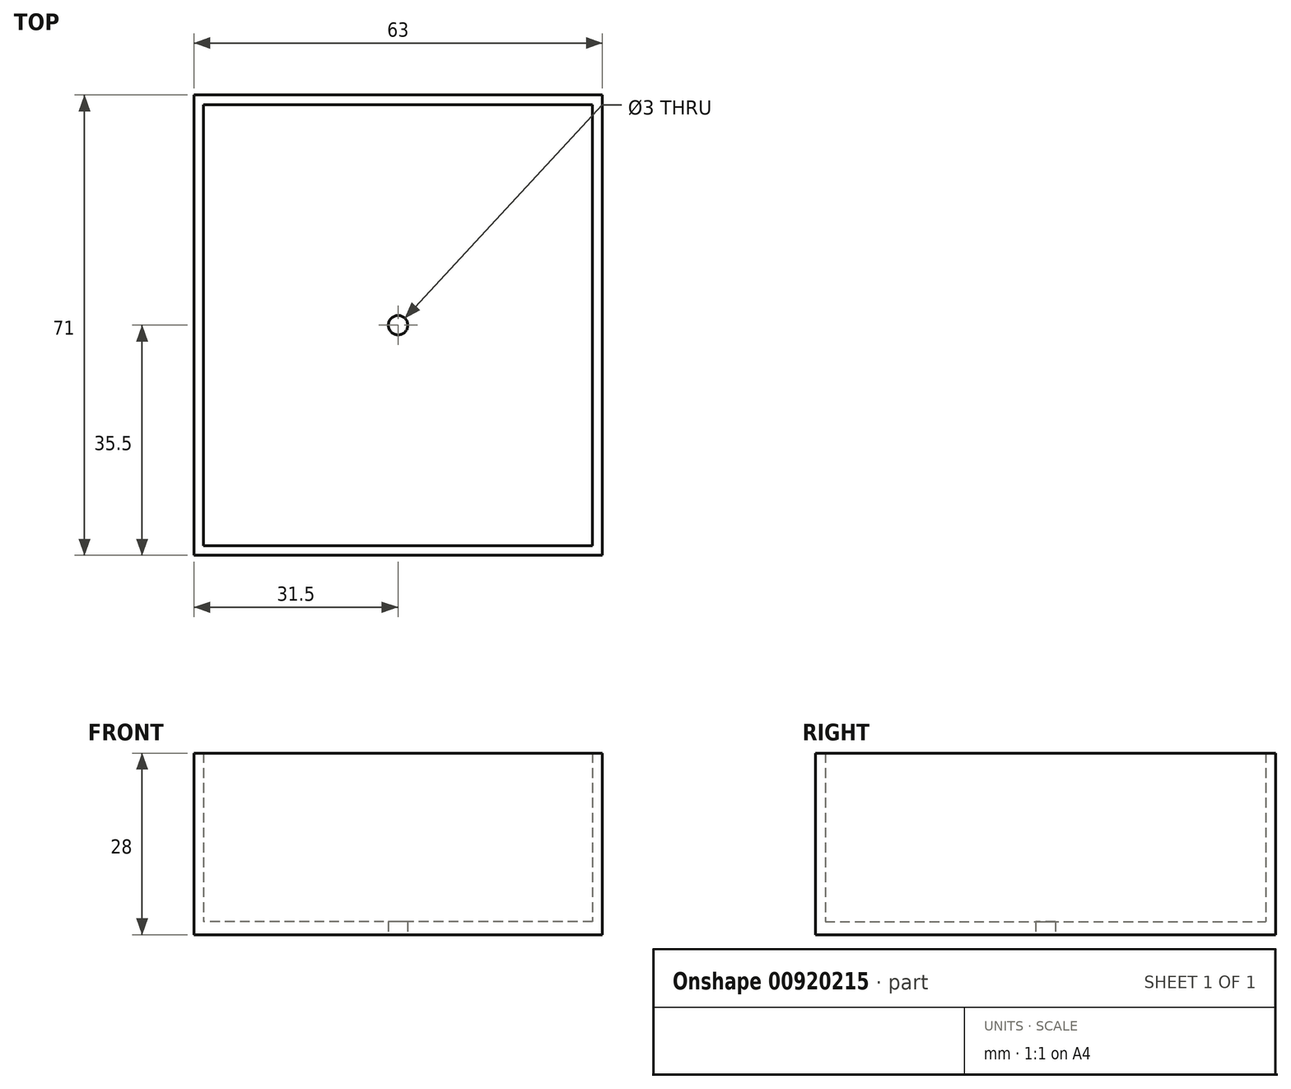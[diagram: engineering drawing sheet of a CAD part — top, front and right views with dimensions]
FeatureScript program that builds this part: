
annotation { "Feature Type Name" : "Feature", "Feature Type Description" : "" }
export const myFeature = defineFeature(function(context is Context, id is Id, definition is map)
    precondition{}
    {
        {
            var Q0;
            Q0=qCreatedBy(makeId("Top.planeOp"),FACE);
            var sketch = newSketch(context, id + "F0", { "sketchPlane" : qUnion([Q0])});
            skLineSegment(sketch, "E0.bottom", {"start": v(-30, 34) * mm, "end": v(30, 34) * mm});
            skLineSegment(sketch, "E0.top", {"start": v(-30, -34) * mm, "end": v(30, -34) * mm});
            skLineSegment(sketch, "E0.left", {"start": v(-30, 34) * mm, "end": v(-30, -34) * mm});
            skLineSegment(sketch, "E0.right", {"start": v(30, 34) * mm, "end": v(30, -34) * mm});
            skPoint(sketch, "E0.middle", {"position": v(0, 0) * mm});
            skLineSegment(sketch, "E1.bottom", {"start": v(-31.5, 35.5) * mm, "end": v(31.5, 35.5) * mm});
            skLineSegment(sketch, "E1.top", {"start": v(-31.5, -35.5) * mm, "end": v(31.5, -35.5) * mm});
            skLineSegment(sketch, "E1.left", {"start": v(-31.5, 35.5) * mm, "end": v(-31.5, -35.5) * mm});
            skLineSegment(sketch, "E1.right", {"start": v(31.5, 35.5) * mm, "end": v(31.5, -35.5) * mm});
            skCircle(sketch, "E2", {"center": v(0, 0) * mm, "radius": 1.5 * mm});
            skSolve(sketch);
        }
        {
            var Q0;
            Q0=makeQuery(id+"F0.imprint","IMPRINT",FACE,{"disambiguationData":[TD([[makeQuery(id+"F0.imprint","IMPRINT",EDGE,{"derivedFrom":sQuery(id+"F0.wireOp",EDGE,"E0.bottom")}),-1.0]])]});
            var Q1;
            Q1=makeQuery(id+"F0.imprint","IMPRINT",FACE,{"disambiguationData":[TD([[makeQuery(id+"F0.imprint","IMPRINT",EDGE,{"derivedFrom":sQuery(id+"F0.wireOp",EDGE,"E0.bottom")}),1.0]])]});
            extrude(context, id + "F1", {"entities" : qUnion([Q0, Q1]), "depth" : 2 * mm, "offsetDistance" : 25 * mm});
        }
        {
            var Q0;
            Q0=makeQuery(id+"F0.imprint","IMPRINT",FACE,{"disambiguationData":[TD([[makeQuery(id+"F0.imprint","IMPRINT",EDGE,{"derivedFrom":sQuery(id+"F0.wireOp",EDGE,"E0.bottom")}),1.0]])]});
            extrude(context, id + "F2", {"entities" : qUnion([Q0]), "operationType" : NewBodyOperationType.ADD, "depth" : 28 * mm, "offsetDistance" : 25 * mm});
        }
    });
